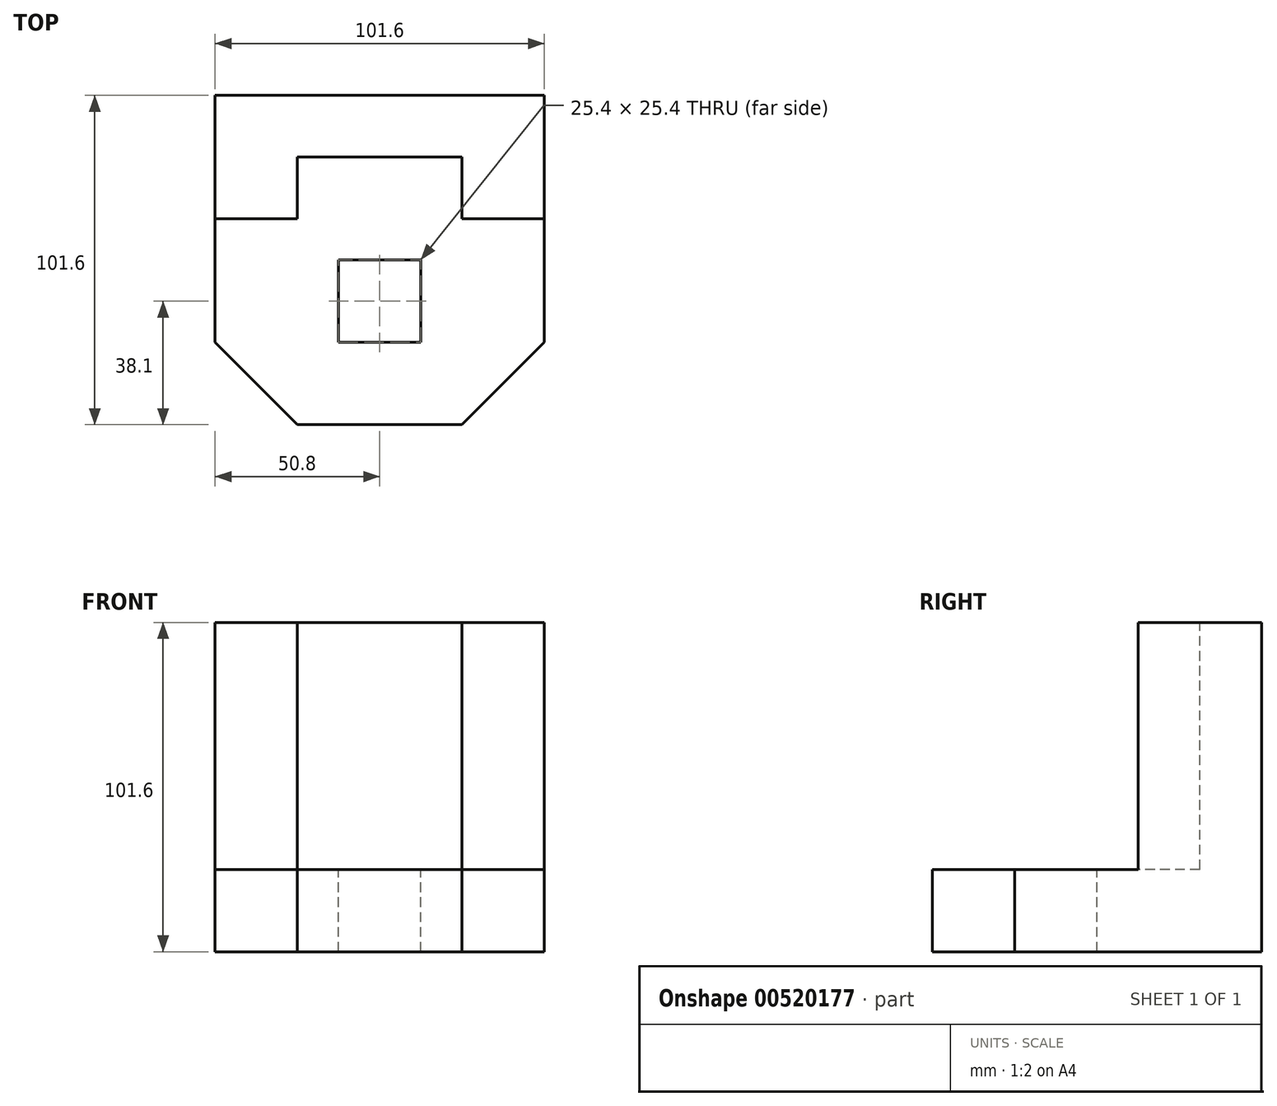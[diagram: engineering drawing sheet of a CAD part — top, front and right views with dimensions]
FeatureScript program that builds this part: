
annotation { "Feature Type Name" : "Feature", "Feature Type Description" : "" }
export const myFeature = defineFeature(function(context is Context, id is Id, definition is map)
    precondition{}
    {
        {
            var Q0;
            Q0=qCreatedBy(makeId("Top.planeOp"),FACE);
            var sketch = newSketch(context, id + "F0", { "sketchPlane" : qUnion([Q0])});
            skLineSegment(sketch, "E0.bottom", {"start": v(0, 0) * mm, "end": v(-101.6, 0) * mm});
            skLineSegment(sketch, "E0.top", {"start": v(0, -101.6) * mm, "end": v(-101.6, -101.6) * mm});
            skLineSegment(sketch, "E0.left", {"start": v(0, 0) * mm, "end": v(0, -101.6) * mm});
            skLineSegment(sketch, "E0.right", {"start": v(-101.6, 0) * mm, "end": v(-101.6, -101.6) * mm});
            skSolve(sketch);
        }
        {
            var Q0;
            Q0 = qSketchRegion(id + "F0", true);
            extrude(context, id + "F1", {"entities" : qUnion([Q0]), "depth" : 101.6 * mm, "offsetDistance" : 25.4 * mm});
        }
        {
            var Q0;
            Q0=makeQuery(id+"F1.opExtrude","CAP_FACE",FACE,{"disambiguationData":[OSD([sQuery(id+"F0.wireOp",EDGE,"E0.bottom"),sQuery(id+"F0.wireOp",EDGE,"E0.top"),sQuery(id+"F0.wireOp",EDGE,"E0.left"),sQuery(id+"F0.wireOp",EDGE,"E0.right")])],"isStart":false});
            var sketch = newSketch(context, id + "F2", { "sketchPlane" : qUnion([Q0])});
            skLineSegment(sketch, "E1.bottom", {"start": v(-101.6, 0) * mm, "end": v(-76.2, 0) * mm});
            skLineSegment(sketch, "E1.top", {"start": v(-101.6, -38.1) * mm, "end": v(-76.2, -38.1) * mm});
            skLineSegment(sketch, "E1.left", {"start": v(-101.6, 0) * mm, "end": v(-101.6, -38.1) * mm});
            skLineSegment(sketch, "E1.right", {"start": v(-76.2, 0) * mm, "end": v(-76.2, -38.1) * mm});
            skLineSegment(sketch, "E2.bottom", {"start": v(0, 0) * mm, "end": v(-25.4, 0) * mm});
            skLineSegment(sketch, "E2.top", {"start": v(0, -38.1) * mm, "end": v(-25.4, -38.1) * mm});
            skLineSegment(sketch, "E2.left", {"start": v(0, 0) * mm, "end": v(0, -38.1) * mm});
            skLineSegment(sketch, "E2.right", {"start": v(-25.4, 0) * mm, "end": v(-25.4, -38.1) * mm});
            skLineSegment(sketch, "E3.bottom", {"start": v(0, 0) * mm, "end": v(-101.6, 0) * mm});
            skLineSegment(sketch, "E3.top", {"start": v(0, -19.05) * mm, "end": v(-101.6, -19.05) * mm});
            skLineSegment(sketch, "E3.left", {"start": v(0, 0) * mm, "end": v(0, -19.05) * mm});
            skLineSegment(sketch, "E3.right", {"start": v(-101.6, 0) * mm, "end": v(-101.6, -19.05) * mm});
            skLineSegment(sketch, "E4", {"start": v(-101.6, -38.1) * mm, "end": v(-101.6, -101.6) * mm});
            skLineSegment(sketch, "E5", {"start": v(-101.6, -101.6) * mm, "end": v(0, -101.6) * mm});
            skLineSegment(sketch, "E6", {"start": v(0, -101.6) * mm, "end": v(0, -38.1) * mm});
            skSolve(sketch);
        }
        {
            var Q0;
            {var subQ5=sQuery(id+"F2.wireOp",EDGE,"E1.top");Q0=makeQuery(id+"F2.imprint","IMPRINT",FACE,{"disambiguationData":[TD([[makeQuery(id+"F2.imprint","IMPRINT",EDGE,{"derivedFrom":subQ5}),-1.0]])]});}
            extrude(context, id + "F3", {"entities" : qUnion([Q0]), "operationType" : NewBodyOperationType.REMOVE, "oppositeDirection" : true, "depth" : 76.2 * mm, "offsetDistance" : 25.4 * mm});
        }
        {
            var Q0;
            Q0=makeQuery(id+"F3.boolean.opBoolean","COPY",FACE,{"derivedFrom":makeQuery(id+"F3.opExtrude","CAP_FACE",FACE,{"disambiguationData":[OSD([sQuery(id+"F2.wireOp",EDGE,"E1.top"),sQuery(id+"F2.wireOp",EDGE,"E1.right"),sQuery(id+"F2.wireOp",EDGE,"E2.top"),sQuery(id+"F2.wireOp",EDGE,"E2.right"),sQuery(id+"F2.wireOp",EDGE,"E3.top"),sQuery(id+"F2.wireOp",EDGE,"E4"),sQuery(id+"F2.wireOp",EDGE,"E5"),sQuery(id+"F2.wireOp",EDGE,"E6")])],"isStart":false})});
            var sketch = newSketch(context, id + "F4", { "sketchPlane" : qUnion([Q0])});
            skLineSegment(sketch, "E7", {"start": v(-101.6, -38.1) * mm, "end": v(-101.6, -76.2) * mm});
            skLineSegment(sketch, "E8", {"start": v(0, -38.1) * mm, "end": v(0, -76.2) * mm});
            skLineSegment(sketch, "E9", {"start": v(-101.6, -101.6) * mm, "end": v(-76.2, -101.6) * mm});
            skLineSegment(sketch, "E10", {"start": v(0, -101.6) * mm, "end": v(-25.4, -101.6) * mm});
            skLineSegment(sketch, "E11", {"start": v(-25.4, -101.6) * mm, "end": v(0, -76.2) * mm});
            skLineSegment(sketch, "E12", {"start": v(-101.6, -76.2) * mm, "end": v(-76.2, -101.6) * mm});
            skLineSegment(sketch, "E13", {"start": v(-101.6, -38.1) * mm, "end": v(-101.6, -50.8) * mm});
            skLineSegment(sketch, "E14", {"start": v(0, -38.1) * mm, "end": v(0, -50.8) * mm});
            skLineSegment(sketch, "E15", {"start": v(0, -50.8) * mm, "end": v(-101.6, -50.8) * mm});
            skLineSegment(sketch, "E16", {"start": v(0, -76.2) * mm, "end": v(-101.6, -76.2) * mm});
            skLineSegment(sketch, "E17", {"start": v(-25.4, -101.6) * mm, "end": v(-38.1, -101.6) * mm});
            skLineSegment(sketch, "E18", {"start": v(-76.2, -101.6) * mm, "end": v(-63.5, -101.6) * mm});
            skLineSegment(sketch, "E19", {"start": v(-63.5, -101.6) * mm, "end": v(-63.5, -19.05) * mm});
            skLineSegment(sketch, "E20", {"start": v(-38.1, -101.6) * mm, "end": v(-38.1, -19.05) * mm});
            skSolve(sketch);
        }
        {
            var Q0;
            {var subQ0=sQuery(id+"F4.wireOp",EDGE,"E20");var subQ1=sQuery(id+"F4.wireOp",EDGE,"E15");var subQ2=makeQuery(id+"F4.imprint","INTERSECT",VERTEX,{"derivedFrom":[subQ1,subQ0]});Q0=makeQuery(id+"F4.imprint","IMPRINT",FACE,{"disambiguationData":[TD([[makeQuery(id+"F4.imprint","IMPRINT",EDGE,{"disambiguationData":[TD([[subQ2,-1.0]])],"derivedFrom":subQ1}),1.0]])]});}
            var Q1;
            {var subQ0=sQuery(id+"F4.wireOp",EDGE,"E10");Q1=makeQuery(id+"F4.imprint","IMPRINT",FACE,{"disambiguationData":[TD([[makeQuery(id+"F4.imprint","IMPRINT",EDGE,{"derivedFrom":subQ0}),-1.0]])]});}
            var Q2;
            {var subQ0=sQuery(id+"F4.wireOp",EDGE,"E9");Q2=makeQuery(id+"F4.imprint","IMPRINT",FACE,{"disambiguationData":[TD([[makeQuery(id+"F4.imprint","IMPRINT",EDGE,{"derivedFrom":subQ0}),-1.0]])]});}
            extrude(context, id + "F5", {"entities" : qUnion([Q0, Q1, Q2]), "operationType" : NewBodyOperationType.REMOVE, "oppositeDirection" : true, "depth" : 25.4 * mm, "offsetDistance" : 25.4 * mm});
        }
    });
